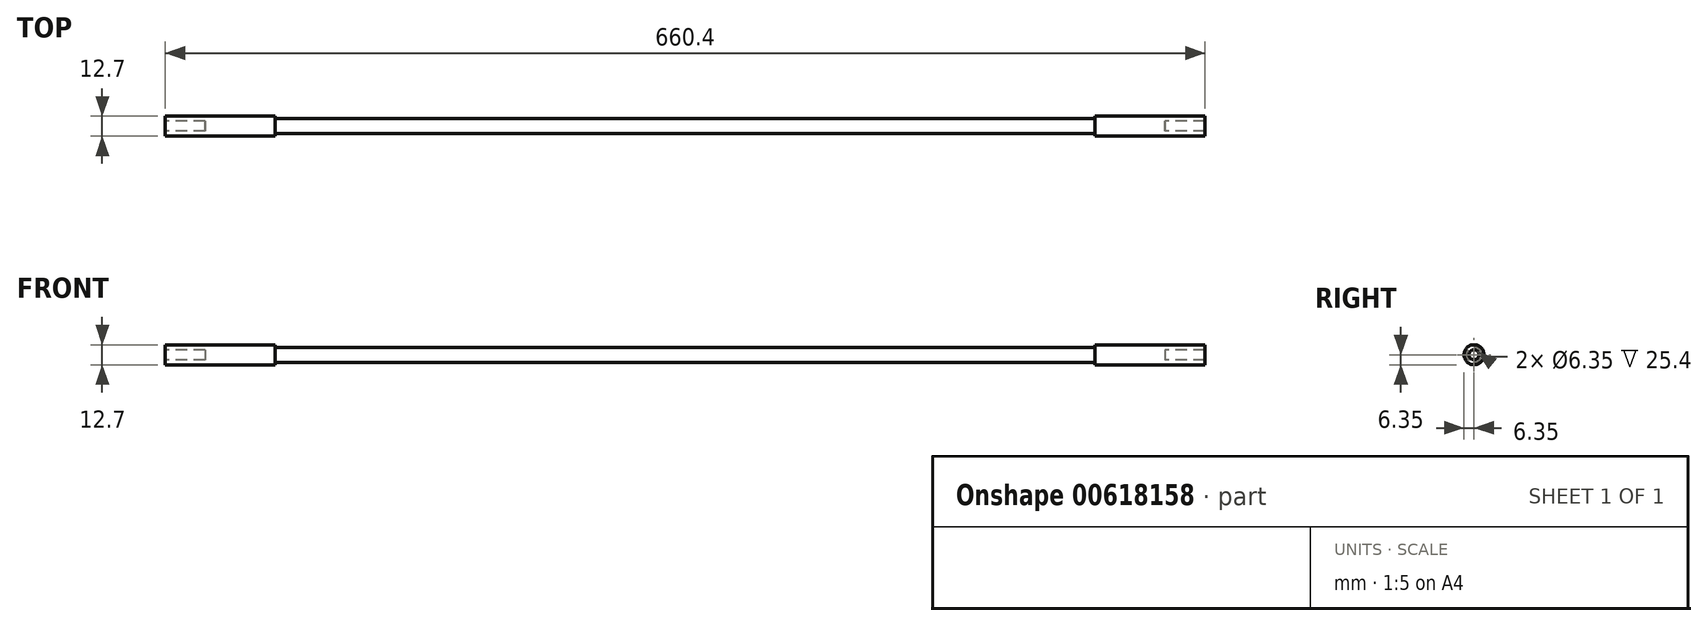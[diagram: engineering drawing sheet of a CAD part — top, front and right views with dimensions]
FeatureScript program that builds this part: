
annotation { "Feature Type Name" : "Feature", "Feature Type Description" : "" }
export const myFeature = defineFeature(function(context is Context, id is Id, definition is map)
    precondition{}
    {
        {
            var Q0;
            Q0=qCreatedBy(makeId("Front.planeOp"),FACE);
            var sketch = newSketch(context, id + "F0", { "sketchPlane" : qUnion([Q0])});
            skLineSegment(sketch, "E0", {"start": v(0, 0) * mm, "end": v(635, 0) * mm});
            skLineSegment(sketch, "E1", {"start": v(25.4, 0) * mm, "end": v(25.4, 3.17) * mm});
            skLineSegment(sketch, "E2", {"start": v(25.4, 3.17) * mm, "end": v(0, 3.17) * mm});
            skLineSegment(sketch, "E3", {"start": v(0, 3.17) * mm, "end": v(0, 6.35) * mm});
            skLineSegment(sketch, "E4", {"start": v(0, 6.35) * mm, "end": v(69.85, 6.35) * mm});
            skLineSegment(sketch, "E5", {"start": v(69.85, 6.35) * mm, "end": v(69.85, 4.76) * mm});
            skLineSegment(sketch, "E6", {"start": v(69.85, 4.76) * mm, "end": v(590.55, 4.76) * mm});
            skLineSegment(sketch, "E7", {"start": v(590.55, 4.76) * mm, "end": v(590.55, 6.35) * mm});
            skLineSegment(sketch, "E8", {"start": v(590.55, 6.35) * mm, "end": v(660.4, 6.35) * mm});
            skLineSegment(sketch, "E9", {"start": v(660.4, 6.35) * mm, "end": v(660.4, 3.18) * mm});
            skLineSegment(sketch, "E10", {"start": v(660.4, 3.18) * mm, "end": v(635, 3.18) * mm});
            skLineSegment(sketch, "E11", {"start": v(635, 3.18) * mm, "end": v(635, 0) * mm});
            skSolve(sketch);
        }
        {
            var Q0;
            Q0=qSketchRegion(id+"F0",true);
            var Q1;
            Q1=sQuery(id+"F0.wireOp",EDGE,"E0");
            revolve(context, id + "F1", {"entities" : qUnion([Q0]), "axis" : qUnion([Q1]), "revolveType" : RevolveType.FULL});
        }
    });
